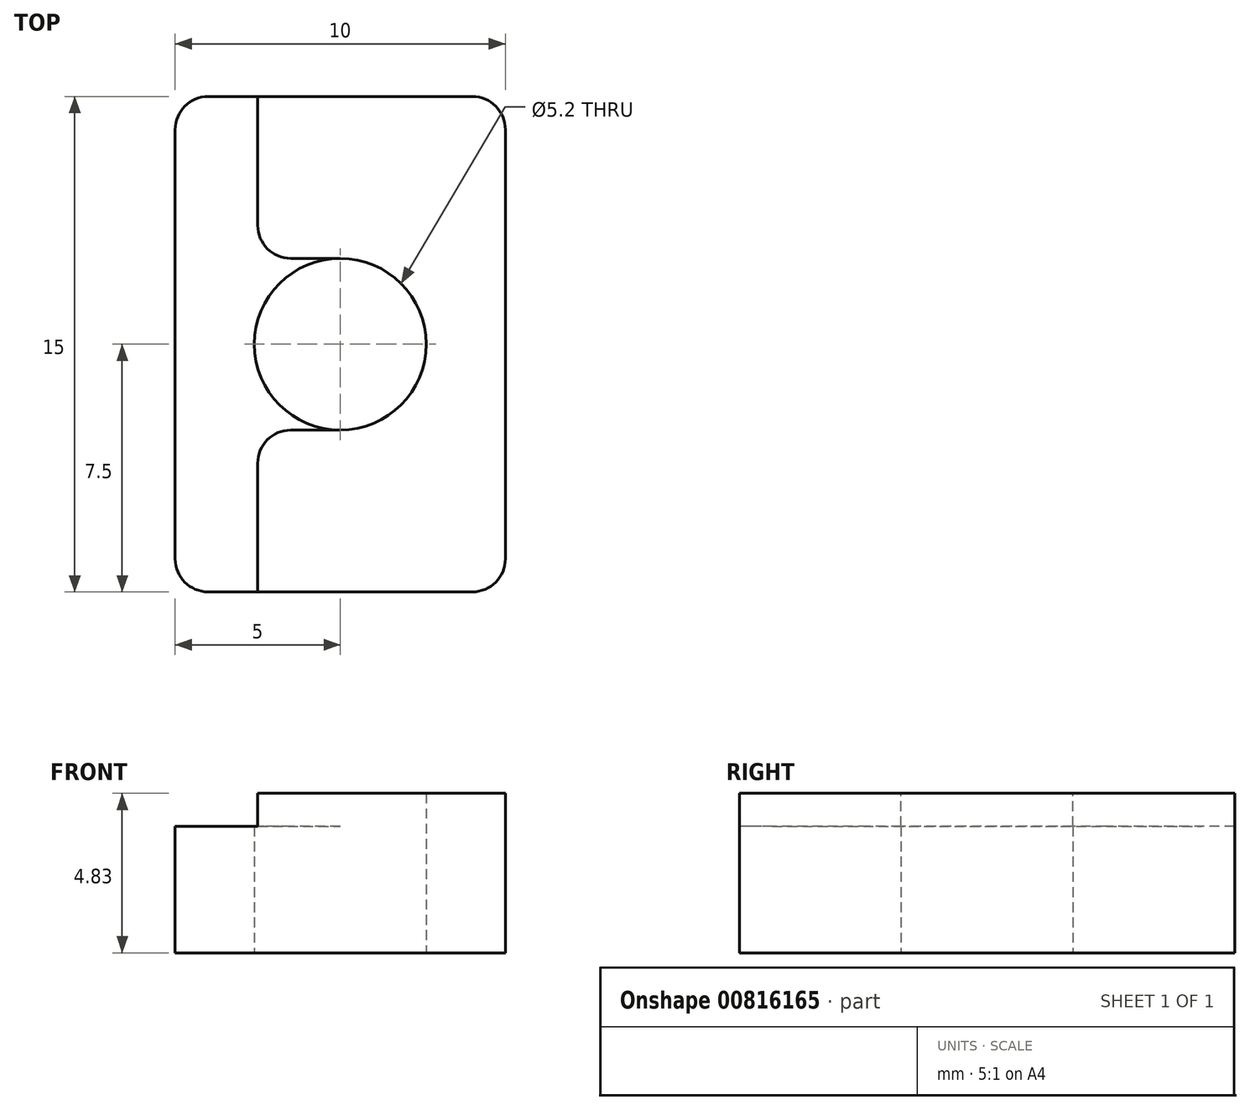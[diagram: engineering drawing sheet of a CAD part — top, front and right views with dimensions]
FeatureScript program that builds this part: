
annotation { "Feature Type Name" : "Feature", "Feature Type Description" : "" }
export const myFeature = defineFeature(function(context is Context, id is Id, definition is map)
    precondition{}
    {
        {
            var Q0;
            Q0=qCreatedBy(makeId("Top.planeOp"),FACE);
            var sketch = newSketch(context, id + "F0", { "sketchPlane" : qUnion([Q0])});
            skCircle(sketch, "E0", {"center": v(0, 0) * mm, "radius": 2.6 * mm});
            skLineSegment(sketch, "E1.bottom", {"start": v(4, -7.5) * mm, "end": v(-4, -7.5) * mm});
            skLineSegment(sketch, "E1.top", {"start": v(4, 7.5) * mm, "end": v(-4, 7.5) * mm});
            skLineSegment(sketch, "E1.left", {"start": v(5, -6.5) * mm, "end": v(5, 6.5) * mm});
            skLineSegment(sketch, "E1.right", {"start": v(-5, -6.5) * mm, "end": v(-5, 6.5) * mm});
            skPoint(sketch, "E2.visualSharp", {"position": v(5, 7.5) * mm});
            skArc(sketch, "E2.filletArc", {"start": v(5, 6.5) * mm, "mid": v(4.7, 7.2) * mm, "end": v(4, 7.5) * mm});
            skPoint(sketch, "E3.visualSharp", {"position": v(5, -7.5) * mm});
            skArc(sketch, "E3.filletArc", {"start": v(4, -7.5) * mm, "mid": v(4.7, -7.2) * mm, "end": v(5, -6.5) * mm});
            skPoint(sketch, "E4.visualSharp", {"position": v(-5, -7.5) * mm});
            skArc(sketch, "E4.filletArc", {"start": v(-5, -6.5) * mm, "mid": v(-4.7, -7.2) * mm, "end": v(-4, -7.5) * mm});
            skPoint(sketch, "E5.visualSharp", {"position": v(-5, 7.5) * mm});
            skArc(sketch, "E5.filletArc", {"start": v(-4, 7.5) * mm, "mid": v(-4.7, 7.2) * mm, "end": v(-5, 6.5) * mm});
            skSolve(sketch);
        }
        {
            var Q0;
            Q0=makeQuery(id+"F0.imprint","IMPRINT",FACE,{"disambiguationData":[TD([[makeQuery(id+"F0.imprint","IMPRINT",EDGE,{"derivedFrom":sQuery(id+"F0.wireOp",EDGE,"E0")}),-1.0]])]});
            extrude(context, id + "F1", {"entities" : qUnion([Q0]), "depth" : 4.83 * mm, "offsetDistance" : 25 * mm});
        }
        {
            var Q0;
            Q0=makeQuery(id+"F1.opExtrude","CAP_FACE",FACE,{"disambiguationData":[OSD([sQuery(id+"F0.wireOp",EDGE,"E0"),sQuery(id+"F0.wireOp",EDGE,"E1.bottom"),sQuery(id+"F0.wireOp",EDGE,"E1.top"),sQuery(id+"F0.wireOp",EDGE,"E1.left"),sQuery(id+"F0.wireOp",EDGE,"E1.right"),sQuery(id+"F0.wireOp",EDGE,"E2.filletArc"),sQuery(id+"F0.wireOp",EDGE,"E3.filletArc"),sQuery(id+"F0.wireOp",EDGE,"E4.filletArc"),sQuery(id+"F0.wireOp",EDGE,"E5.filletArc")])],"isStart":false});
            var sketch = newSketch(context, id + "F2", { "sketchPlane" : qUnion([Q0])});
            skLineSegment(sketch, "E6.bottom", {"start": v(-2.5, 10) * mm, "end": v(-7.5, 10) * mm});
            skLineSegment(sketch, "E6.top", {"start": v(-2.5, -10) * mm, "end": v(-7.5, -10) * mm});
            skLineSegment(sketch, "E6.left", {"start": v(-2.5, 10) * mm, "end": v(-2.5, 2.6) * mm});
            skLineSegment(sketch, "E6.right", {"start": v(-7.5, 10) * mm, "end": v(-7.5, -10) * mm});
            skPoint(sketch, "E6.middle", {"position": v(-5, 0) * mm});
            skCircle(sketch, "E7", {"center": v(0, 0) * mm, "radius": 2.6 * mm});
            skLineSegment(sketch, "E8.bottom", {"start": v(0, 2.6) * mm, "end": v(-2.5, 2.6) * mm});
            skLineSegment(sketch, "E8.top", {"start": v(0, -2.6) * mm, "end": v(-2.5, -2.6) * mm});
            skPoint(sketch, "E9.orphan", {"position": v(2.6, 2.6) * mm});
            skPoint(sketch, "E10.orphan", {"position": v(2.6, -2.6) * mm});
            skLineSegment(sketch, "E11.trimOffspring", {"start": v(-2.5, -2.6) * mm, "end": v(-2.5, -10) * mm});
            skPoint(sketch, "E12.orphan", {"position": v(-2.6, 2.6) * mm});
            skPoint(sketch, "E13.orphan", {"position": v(-2.6, -2.6) * mm});
            skSolve(sketch);
        }
        {
            var Q0;
            Q0=makeQuery(id+"F2.imprint","IMPRINT",FACE,{"disambiguationData":[TD([[makeQuery(id+"F2.imprint","IMPRINT",EDGE,{"derivedFrom":makeQuery(id+"F1.opExtrude","CAP_EDGE",EDGE,{"disambiguationData":[OSD([sQuery(id+"F0.wireOp",EDGE,"E1.right")])],"isStart":false})}),-1.0]])]});
            extrude(context, id + "F3", {"entities" : qUnion([Q0]), "operationType" : NewBodyOperationType.REMOVE, "oppositeDirection" : true, "depth" : 1 * mm, "offsetDistance" : 25 * mm});
        }
        {
            var Q0;
            Q0=makeQuery(id+"F3.boolean.opBoolean","COPY",EDGE,{"derivedFrom":makeQuery(id+"F3.opExtrude","SWEPT_EDGE",EDGE,{"disambiguationData":[OSD([sQuery(id+"F0.wireOp",EDGE,"E1.bottom"),sQuery(id+"F2.wireOp",EDGE,"E11.trimOffspring")])]})});
            var Q1;
            Q1=makeQuery(id+"F3.boolean.opBoolean","COPY",EDGE,{"derivedFrom":makeQuery(id+"F3.opExtrude","SWEPT_EDGE",EDGE,{"disambiguationData":[OSD([sQuery(id+"F2.wireOp",EDGE,"E6.left"),sQuery(id+"F2.wireOp",EDGE,"E8.bottom")])]})});
            var Q2;
            Q2=makeQuery(id+"F3.boolean.opBoolean","COPY",EDGE,{"derivedFrom":makeQuery(id+"F3.opExtrude","SWEPT_EDGE",EDGE,{"disambiguationData":[OSD([sQuery(id+"F2.wireOp",EDGE,"E8.top"),sQuery(id+"F2.wireOp",EDGE,"E11.trimOffspring")])]})});
            var Q3;
            Q3=makeQuery(id+"F3.boolean.opBoolean","COPY",EDGE,{"derivedFrom":makeQuery(id+"F3.opExtrude","SWEPT_EDGE",EDGE,{"disambiguationData":[OSD([sQuery(id+"F0.wireOp",EDGE,"E1.top"),sQuery(id+"F2.wireOp",EDGE,"E6.left")])]})});
            fillet(context, id + "F4", {"entities" : qUnion([Q0, Q1, Q2, Q3]), "radius" : 1 * mm, "tangentPropagation" : true, "allowEdgeOverflow" : false});
        }
    });
